# Revit family: GP_ДП_R15
name_source: partatom
category: Обобщенные модели
revit_build: Autodesk Revit 2015 (Build: 20140322_1515(x64)
units: mm (PartAtom-declared; Revit-internal decimal feet)

## types (4) — shared parameters
ADSK_URL страницы изделия = http://gbi-podolsk.ru
GP_Адрес = Московская область, г. Подольск, ул. Шамотная, д. 11А
GP_Контактный телефон = ‎8-495-999-46-60, ‎8-916-155-11-85
GP_Логотип компании = Логотип.jpg
Изготовитель = ООО «Компания Фурор-Строй»
Изображение типоразмера = ДП.png
Описание = Дорожная плита
zero-valued in all types: Стоимость

## per-type parameters (varying)
| type | ADSK_Материал | ADSK_Наименование | ADSK_Размер_Высота | ADSK_Размер_Длина | ADSK_Размер_Ширина | GP_Водонепроницаемость | GP_Масса | GP_Морозостойкость | GP_Объем | GP_Прочность |
| 2П30.18.30 | Бетон_B22.5_F150_W2 | Плита дорожная 2П30.18.30 | 170 мм | 3000 мм | 1750 мм | W2 | 2.20 t | F150 | 0.88 м³ | B22.5 |
| ПАГ-14 | Бетон_B30_F200_W6 | Плита дорожная ПАГ-14 | 140 мм | 6000 мм | 2000 мм | W6 | 4.20 t | F200 | 1.68 м³ | B30 |
| ПАГ-18 | Бетон_B30_F200_W6 | Плита дорожная ПАГ-18 | 180 мм | 6000 мм | 2000 мм | W6 | 5.40 t | F200 | 2.16 м³ | B30 |
| ПДН | Бетон_B30_F200_W6 | Плита дорожная ПДН | 140 мм | 6000 мм | 2000 мм | W6 | 4.20 t | F200 | 1.68 м³ | B30 |

note: column(s) folded — value = type name in every type: ADSK_Марка
